# Revit family: Lighting_Fixture-Wall-Astro-Bergamo600
name_source: partatom
category: Lighting Fixtures
revit_build: Autodesk Revit 2014 (Build: 20130308_1515(x64)
units: mm (PartAtom-declared; Revit-internal decimal feet)

## types (1)
- Type 1
    Apparent Load = 18 VA
    Assembly Code = D5020200
    Class = 2
    Color Filter = 16777215
    Description = Mirror Light
    Dimmable = No
    Dimming Lamp Color Temperature Shift = <None>
    Emit Shape Visible in Rendering = No
    Emit from Rectangle Length = 550 mm
    Emit from Rectangle Width = 55 mm  [stored 0.180446 ft]
    End Casing Material = Astro - Zinc - Chrome Finish
    Energy Efficiency Rating = -
    Front Casing Material = Astro - Aluminium - Chrome Finish
    Height = 55 mm  [stored 0.180446 ft]
    IP Rating = IP44
    Lamp = LED
    Lamp included = No
    Length = 53 mm  [stored 0.173885 ft]
    Light Source Elevation = 1600 mm  [stored 5.24934 ft]
    Light Source From Wall = 44 mm  [stored 0.144357 ft]
    Luminaire Lamp Efficiency Rating = A
    Manufacturer = Astro Lighting Ltd, CM20 2DP
    Model = 0893 Bergamo 600
    Mountable on normally flammable surfaces = Yes
    Number of Poles = 1
    Photometric Web File = 0893 BERGAMO 600.ies
    Product Documentation = http://www.astrolighting.co.uk
/kw/bergamo/0893_Bergamo-600
    Suitable for bathroom zone = Zones 2, 3
    Tilt Angle = 90.00°
    Type Comments = - Can be mounted vertically or horizontally
 - Includes internal electronic driver
    URL = www.astrolighting.co.uk
    Voltage = 230 V
    Wall Bracket Material = Astro - Steel - Chrome Finish
    Wattage Comments = 15.4W
    Weight = 1.4 kg
    Width = 600 mm

note: [stored X ft] marks values corroborated as IEEE doubles in the binary element streams (Revit-internal decimal feet)

## geometry (parser evidence)
native form markers: Sweep x1
no freeform markers — native parametric forms only
